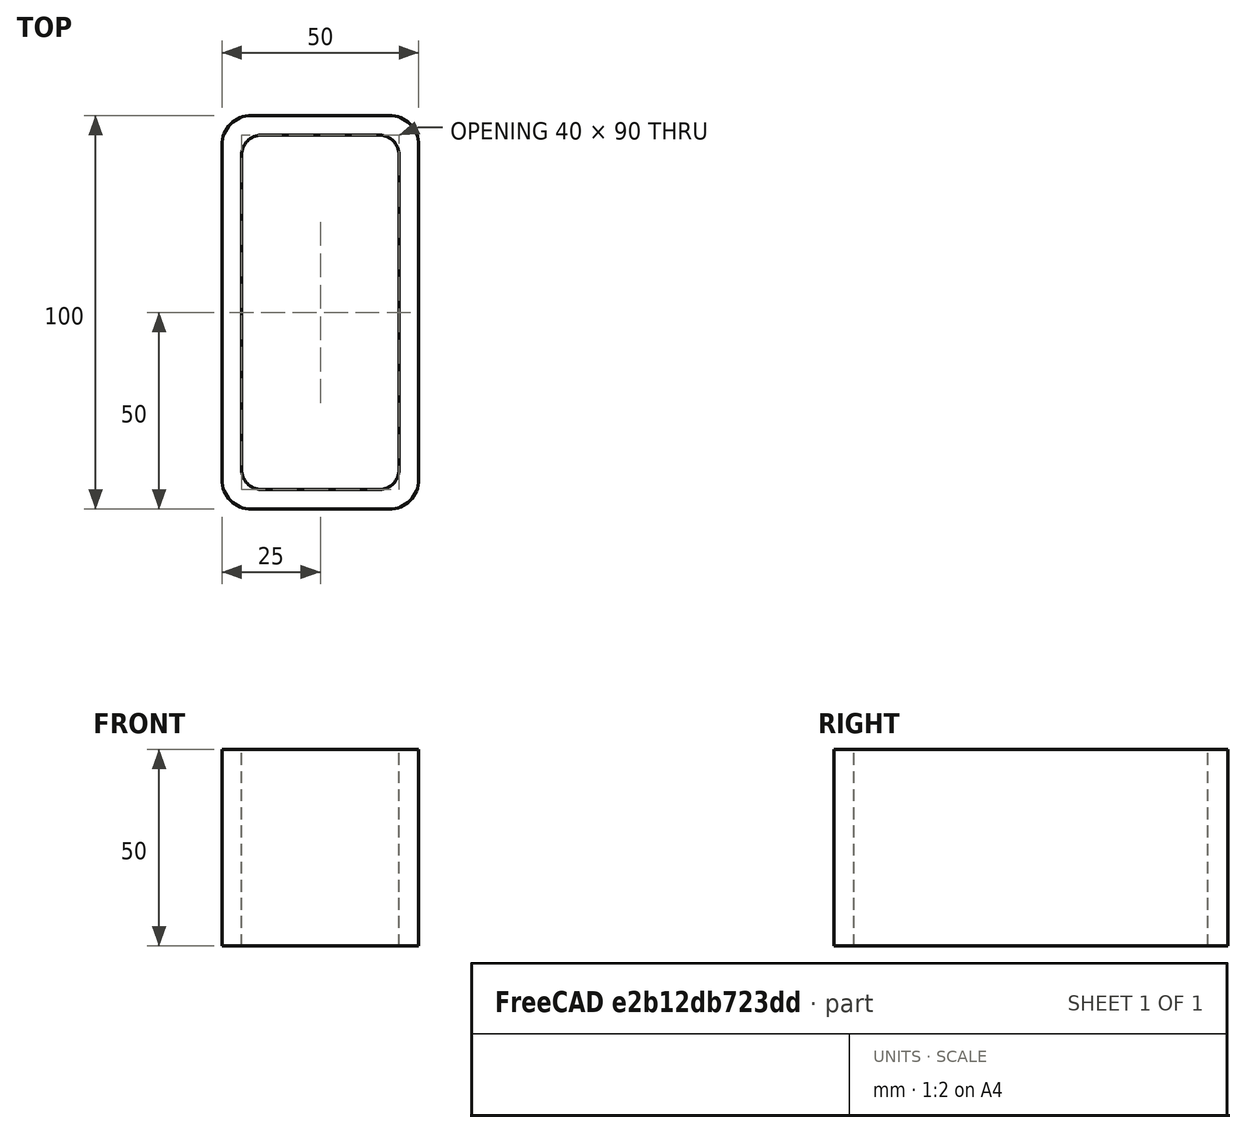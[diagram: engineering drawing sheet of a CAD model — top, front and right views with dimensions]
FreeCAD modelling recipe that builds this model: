
FCSTD DOCUMENT  (FreeCAD 0.15R4671 (Git))
Label: Rectangular hollow section 100x50x5 EN10219 S235JRH
License: All rights reserved
LicenseURL: http://en.wikipedia.org/wiki/All_rights_reserved
objects: Sketcher::SketchObject×1, Part::Extrusion×1
note: 2 computed .brp shape members not serialized (recipe doc carries the construction recipe); baked Part::Feature solids carry a one-line shape summary decoded from their .brp

FEATURE [Sketcher::SketchObject] Sketch
  sketch-geometry (16):
    g0: LineSegment StartX=-15 StartY=45 StartZ=0 EndX=15 EndY=45 EndZ=0
    g1: LineSegment StartX=20 StartY=40 StartZ=0 EndX=20 EndY=-40 EndZ=0
    g2: LineSegment StartX=15 StartY=-45 StartZ=0 EndX=-15 EndY=-45 EndZ=0
    g3: LineSegment StartX=-20 StartY=-40 StartZ=0 EndX=-20 EndY=40 EndZ=0
    g4: LineSegment StartX=-17.5 StartY=50 StartZ=0 EndX=17.5 EndY=50 EndZ=0
    g5: LineSegment StartX=25 StartY=42.5 StartZ=0 EndX=25 EndY=-42.5 EndZ=0
    g6: LineSegment StartX=17.5 StartY=-50 StartZ=0 EndX=-17.5 EndY=-50 EndZ=0
    g7: LineSegment StartX=-25 StartY=-42.5 StartZ=0 EndX=-25 EndY=42.5 EndZ=0
    g8: ArcOfCircle CenterX=-15 CenterY=40 CenterZ=0 NormalX=0 NormalY=0 NormalZ=1 Radius=5 StartAngle=1.5708 EndAngle=3.14159
    g9: ArcOfCircle CenterX=15 CenterY=40 CenterZ=0 NormalX=0 NormalY=0 NormalZ=1 Radius=5 StartAngle=0 EndAngle=1.5708
    g10: ArcOfCircle CenterX=15 CenterY=-40 CenterZ=0 NormalX=0 NormalY=0 NormalZ=1 Radius=5 StartAngle=4.71239 EndAngle=6.28319
    g11: ArcOfCircle CenterX=-15 CenterY=-40 CenterZ=0 NormalX=0 NormalY=0 NormalZ=1 Radius=5 StartAngle=3.14159 EndAngle=4.71239
    g12: ArcOfCircle CenterX=17.5 CenterY=42.5 CenterZ=0 NormalX=0 NormalY=0 NormalZ=1 Radius=7.5 StartAngle=0 EndAngle=1.5708
    g13: ArcOfCircle CenterX=17.5 CenterY=-42.5 CenterZ=0 NormalX=0 NormalY=0 NormalZ=1 Radius=7.5 StartAngle=4.71239 EndAngle=6.28319
    g14: ArcOfCircle CenterX=-17.5 CenterY=-42.5 CenterZ=0 NormalX=0 NormalY=0 NormalZ=1 Radius=7.5 StartAngle=3.14159 EndAngle=4.71239
    g15: ArcOfCircle CenterX=-17.5 CenterY=42.5 CenterZ=0 NormalX=0 NormalY=0 NormalZ=1 Radius=7.5 StartAngle=1.5708 EndAngle=3.14159
  constraints (36):
    c: Horizontal(g2)
    c: Vertical(g3)
    c: Horizontal(g6)
    c: Vertical(g7)
    c: Tangent(g3,g8) = 1.5708
    c: Tangent(g0,g8) = 1.5708
    c: Tangent(g0,g9) = 1.5708
    c: Tangent(g1,g9) = 1.5708
    c: Tangent(g1,g10) = 1.5708
    c: Tangent(g2,g10) = 1.5708
    c: Tangent(g2,g11) = 1.5708
    c: Tangent(g3,g11) = 1.5708
    c: Tangent(g4,g12) = 1.5708
    c: Tangent(g5,g12) = 1.5708
    c: Tangent(g5,g13) = 1.5708
    c: Tangent(g6,g13) = 1.5708
    c: Tangent(g6,g14) = 1.5708
    c: Tangent(g7,g14) = 1.5708
    c: Tangent(g7,g15) = 1.5708
    c: Tangent(g4,g15) = 1.5708
    c: Equal(g9,g8)
    c: Equal(g9,g11)
    c: Equal(g9,g10)
    c: Equal(g12,g15)
    c: Equal(g12,g14)
    c: Equal(g12,g13)
    c: Symmetric(g4,g6,g-1)
    c: Symmetric(g7,g5,g-2)
    c: DistanceY(g4,g6) = -100
    c: DistanceX(g7,g5) = 50
    c: Symmetric(g3,g1,g-2)
    c: Symmetric(g0,g2,g-1)
    c: DistanceY(g0,g4) = 5
    c: DistanceX(g5,g1) = -5
    c: Radius(g9) = 5
    c: Radius(g12) = 7.5
FEATURE [Part::Extrusion] Extrude  label="Rectangular hollow section 100x50x5 EN10219 S235JRH"
  Base = -> Sketch
  Dir = (0,0,50)
  Solid = true
